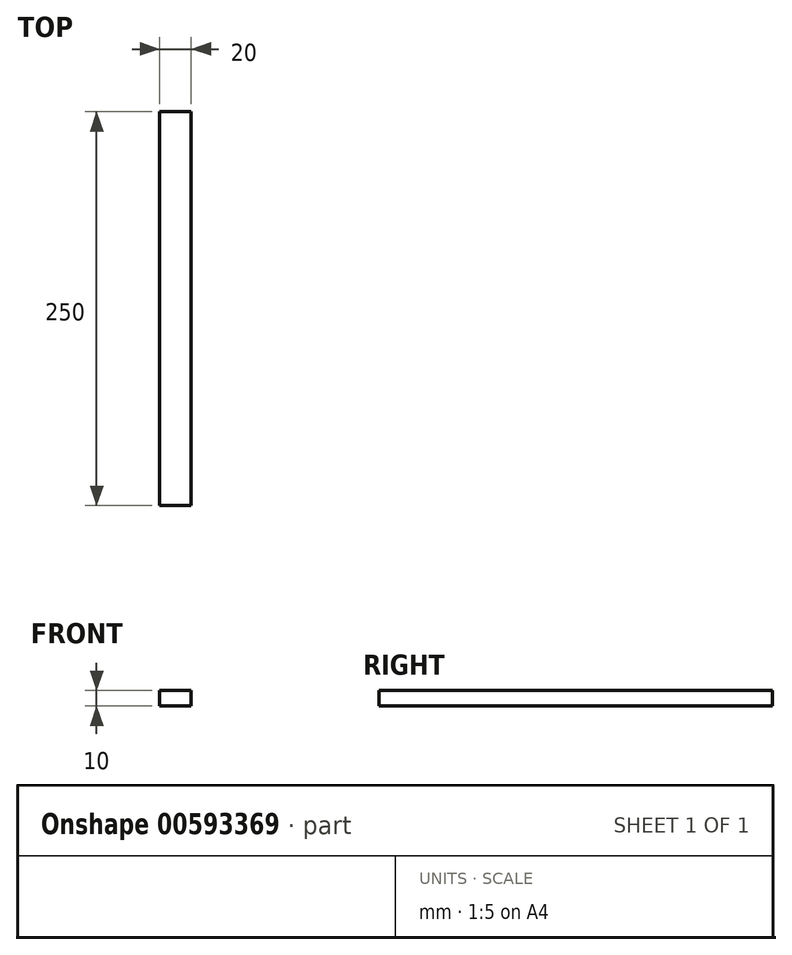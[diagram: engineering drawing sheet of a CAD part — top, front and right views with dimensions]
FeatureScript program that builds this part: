
annotation { "Feature Type Name" : "Feature", "Feature Type Description" : "" }
export const myFeature = defineFeature(function(context is Context, id is Id, definition is map)
    precondition{}
    {
        {
            var Q0;
            Q0=qCreatedBy(makeId("Top.planeOp"),FACE);
            var sketch = newSketch(context, id + "F0", { "sketchPlane" : qUnion([Q0])});
            skLineSegment(sketch, "E0.bottom", {"start": v(-13.94, 220.92) * mm, "end": v(6.06, 220.92) * mm});
            skLineSegment(sketch, "E0.top", {"start": v(-13.94, -29.08) * mm, "end": v(6.06, -29.08) * mm});
            skLineSegment(sketch, "E0.left", {"start": v(-13.94, 220.92) * mm, "end": v(-13.94, -29.08) * mm});
            skLineSegment(sketch, "E0.right", {"start": v(6.06, 220.92) * mm, "end": v(6.06, -29.08) * mm});
            skSolve(sketch);
        }
        {
            var Q0;
            Q0=makeQuery(id+"F0.imprint","IMPRINT",FACE,{"disambiguationData":[TD([[makeQuery(id+"F0.imprint","IMPRINT",EDGE,{"derivedFrom":sQuery(id+"F0.wireOp",EDGE,"E0.bottom")}),-1.0]])]});
            extrude(context, id + "F1", {"entities" : qUnion([Q0]), "depth" : 10 * mm, "offsetDistance" : 25.4 * mm});
        }
    });
